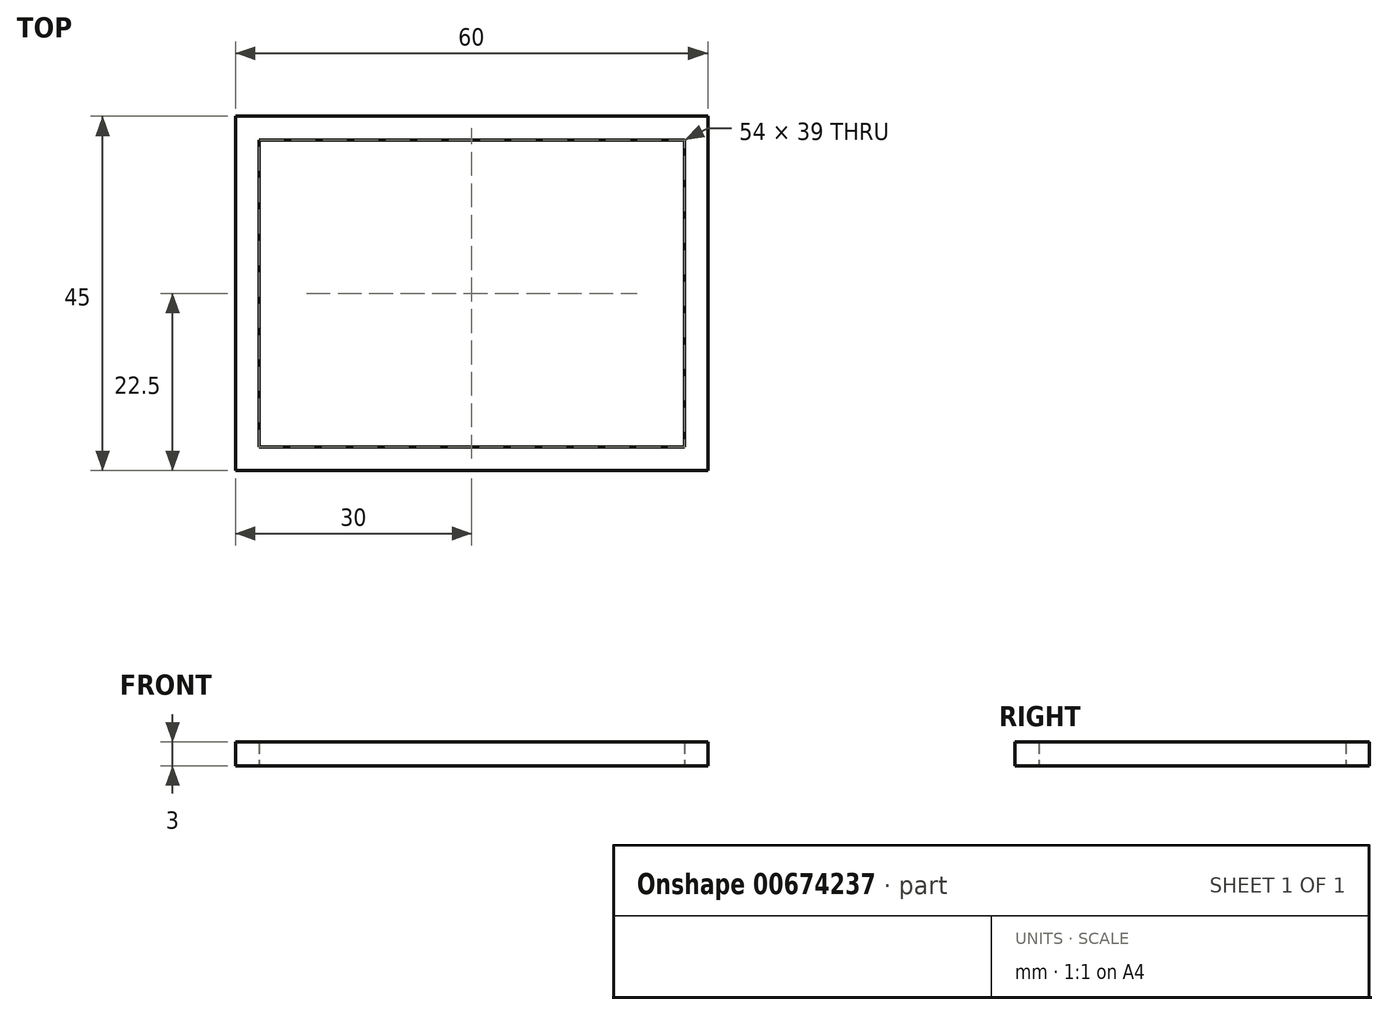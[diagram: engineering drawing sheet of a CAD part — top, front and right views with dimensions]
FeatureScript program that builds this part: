
annotation { "Feature Type Name" : "Feature", "Feature Type Description" : "" }
export const myFeature = defineFeature(function(context is Context, id is Id, definition is map)
    precondition{}
    {
        {
            var Q0;
            Q0=qCreatedBy(makeId("Top.planeOp"),FACE);
            var sketch = newSketch(context, id + "F0", { "sketchPlane" : qUnion([Q0])});
            skLineSegment(sketch, "E0.bottom", {"start": v(30, 22.5) * mm, "end": v(-30, 22.5) * mm});
            skLineSegment(sketch, "E0.top", {"start": v(30, -22.5) * mm, "end": v(-30, -22.5) * mm});
            skLineSegment(sketch, "E0.left", {"start": v(30, 22.5) * mm, "end": v(30, -22.5) * mm});
            skLineSegment(sketch, "E0.right", {"start": v(-30, 22.5) * mm, "end": v(-30, -22.5) * mm});
            skPoint(sketch, "E0.middle", {"position": v(0, 0) * mm});
            skLineSegment(sketch, "E1.0", {"start": v(27, 19.5) * mm, "end": v(-27, 19.5) * mm});
            skLineSegment(sketch, "E1.1", {"start": v(27, 19.5) * mm, "end": v(27, -19.5) * mm});
            skLineSegment(sketch, "E1.2", {"start": v(27, -19.5) * mm, "end": v(-27, -19.5) * mm});
            skLineSegment(sketch, "E1.3", {"start": v(-27, 19.5) * mm, "end": v(-27, -19.5) * mm});
            skSolve(sketch);
        }
        {
            var Q0;
            Q0 = qSketchRegion(id + "F0", true);
            extrude(context, id + "F1", {"entities" : qUnion([Q0]), "depth" : 3 * mm, "offsetDistance" : 25 * mm});
        }
    });
